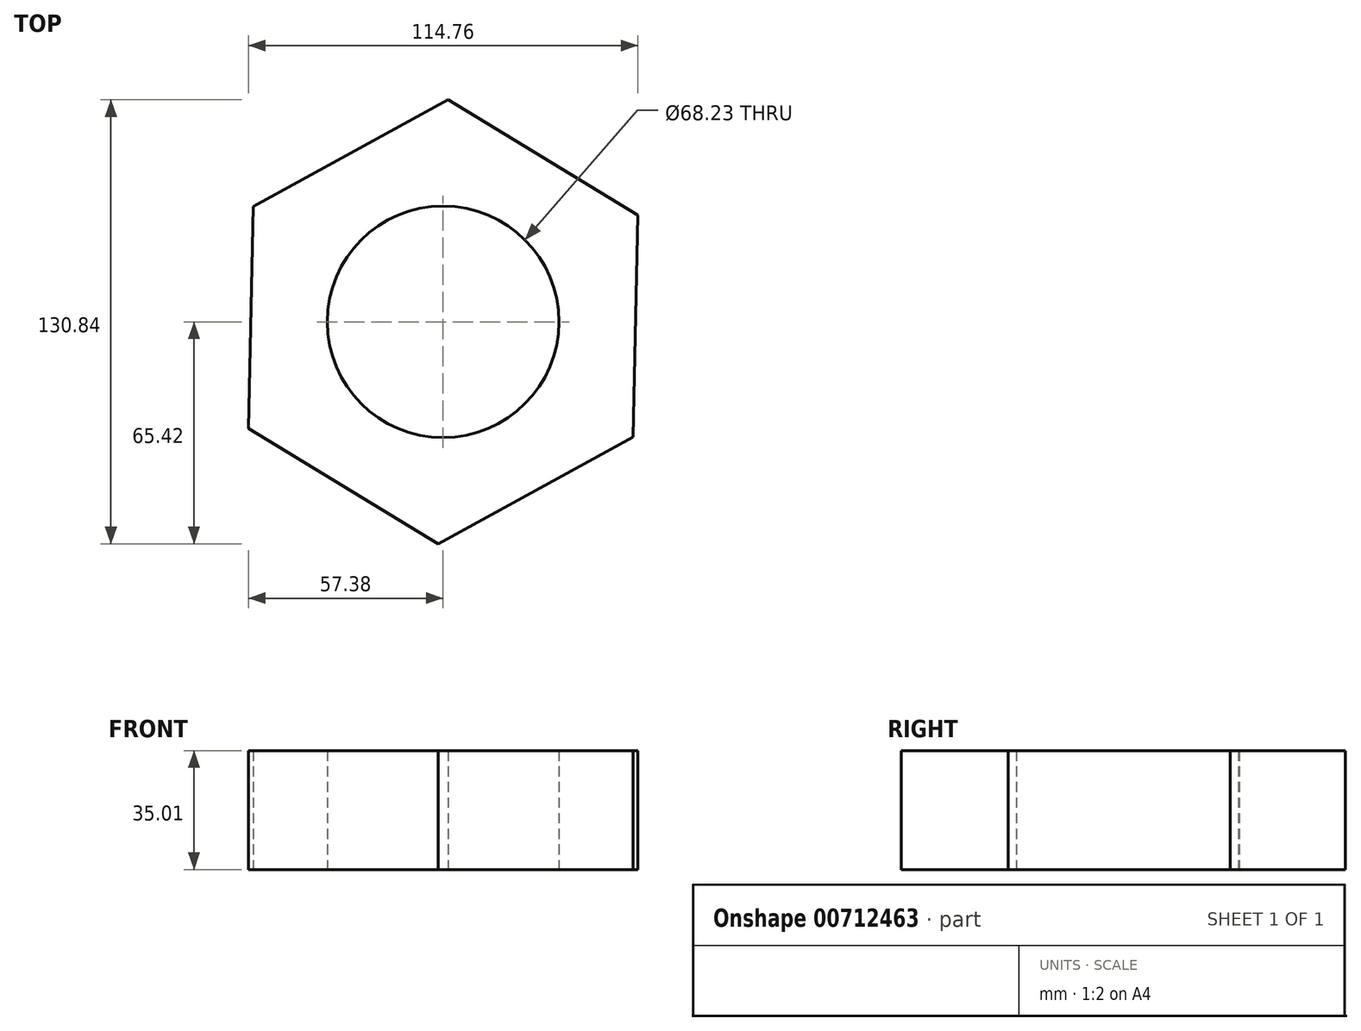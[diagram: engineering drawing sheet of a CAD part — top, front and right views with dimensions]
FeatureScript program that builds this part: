
annotation { "Feature Type Name" : "Feature", "Feature Type Description" : "" }
export const myFeature = defineFeature(function(context is Context, id is Id, definition is map)
    precondition{}
    {
        {
            var Q0;
            Q0=qCreatedBy(makeId("Top.planeOp"),FACE);
            var sketch = newSketch(context, id + "F0", { "sketchPlane" : qUnion([Q0])});
            skCircle(sketch, "E0.cCircle", {"center": v(0, 0) * mm, "radius": 65.44 * mm, "construction": true});
            skLineSegment(sketch, "E0.0", {"start": v(55.94, -33.96) * mm, "end": v(-1.44, -65.42) * mm});
            skLineSegment(sketch, "E0.1", {"start": v(-1.44, -65.42) * mm, "end": v(-57.38, -31.46) * mm});
            skLineSegment(sketch, "E0.2", {"start": v(-57.38, -31.46) * mm, "end": v(-55.94, 33.96) * mm});
            skLineSegment(sketch, "E0.3", {"start": v(-55.94, 33.96) * mm, "end": v(1.44, 65.42) * mm});
            skLineSegment(sketch, "E0.4", {"start": v(1.44, 65.42) * mm, "end": v(57.38, 31.46) * mm});
            skLineSegment(sketch, "E0.5", {"start": v(57.38, 31.46) * mm, "end": v(55.94, -33.96) * mm});
            skCircle(sketch, "E1", {"center": v(0, 0) * mm, "radius": 34.11 * mm});
            skSolve(sketch);
        }
        {
            var Q0;
            Q0=makeQuery(id+"F0.imprint","IMPRINT",FACE,{"disambiguationData":[TD([[makeQuery(id+"F0.imprint","IMPRINT",EDGE,{"derivedFrom":sQuery(id+"F0.wireOp",EDGE,"E0.0")}),-1.0]])]});
            extrude(context, id + "F1", {"entities" : qUnion([Q0]), "depth" : 35 * mm, "offsetDistance" : 25.4 * mm});
        }
    });
